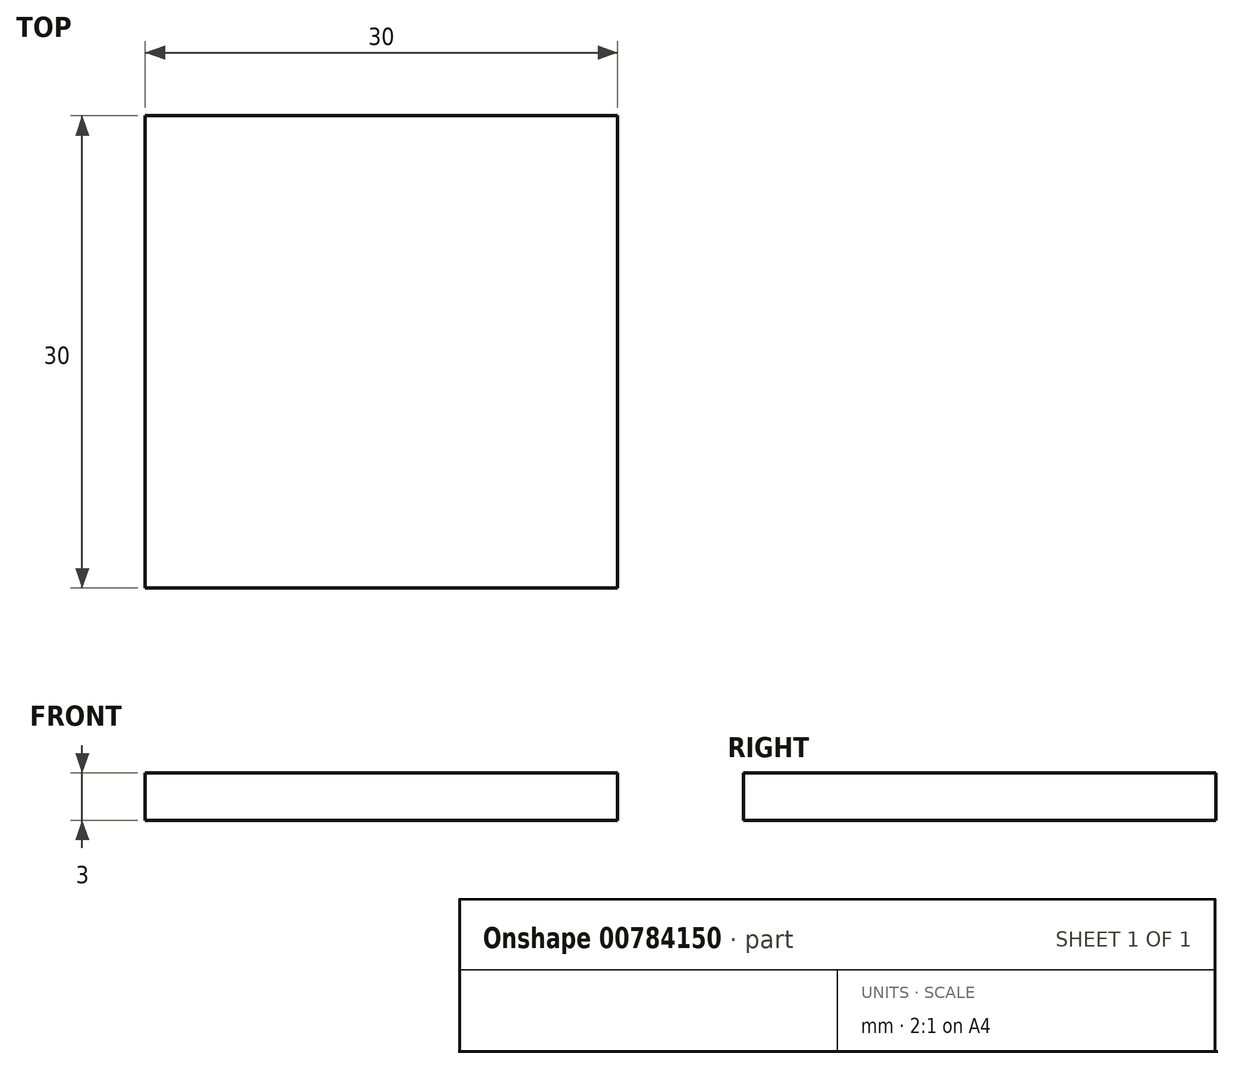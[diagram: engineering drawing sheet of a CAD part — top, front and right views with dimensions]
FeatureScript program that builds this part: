
annotation { "Feature Type Name" : "Feature", "Feature Type Description" : "" }
export const myFeature = defineFeature(function(context is Context, id is Id, definition is map)
    precondition{}
    {
        {
            var Q0;
            Q0=qCreatedBy(makeId("Top.planeOp"),FACE);
            var sketch = newSketch(context, id + "F0", { "sketchPlane" : qUnion([Q0])});
            skLineSegment(sketch, "E0.bottom", {"start": v(15, 15) * mm, "end": v(-15, 15) * mm});
            skLineSegment(sketch, "E0.top", {"start": v(15, -15) * mm, "end": v(-15, -15) * mm});
            skLineSegment(sketch, "E0.left", {"start": v(15, 15) * mm, "end": v(15, -15) * mm});
            skLineSegment(sketch, "E0.right", {"start": v(-15, 15) * mm, "end": v(-15, -15) * mm});
            skPoint(sketch, "E0.middle", {"position": v(0, 0) * mm});
            skSolve(sketch);
        }
        {
            var Q0;
            Q0=makeQuery(id+"F0.imprint","IMPRINT",FACE,{"disambiguationData":[TD([[makeQuery(id+"F0.imprint","IMPRINT",EDGE,{"derivedFrom":sQuery(id+"F0.wireOp",EDGE,"E0.bottom")}),1.0]])]});
            extrude(context, id + "F1", {"entities" : qUnion([Q0]), "depth" : 3 * mm, "offsetDistance" : 25 * mm});
        }
    });
